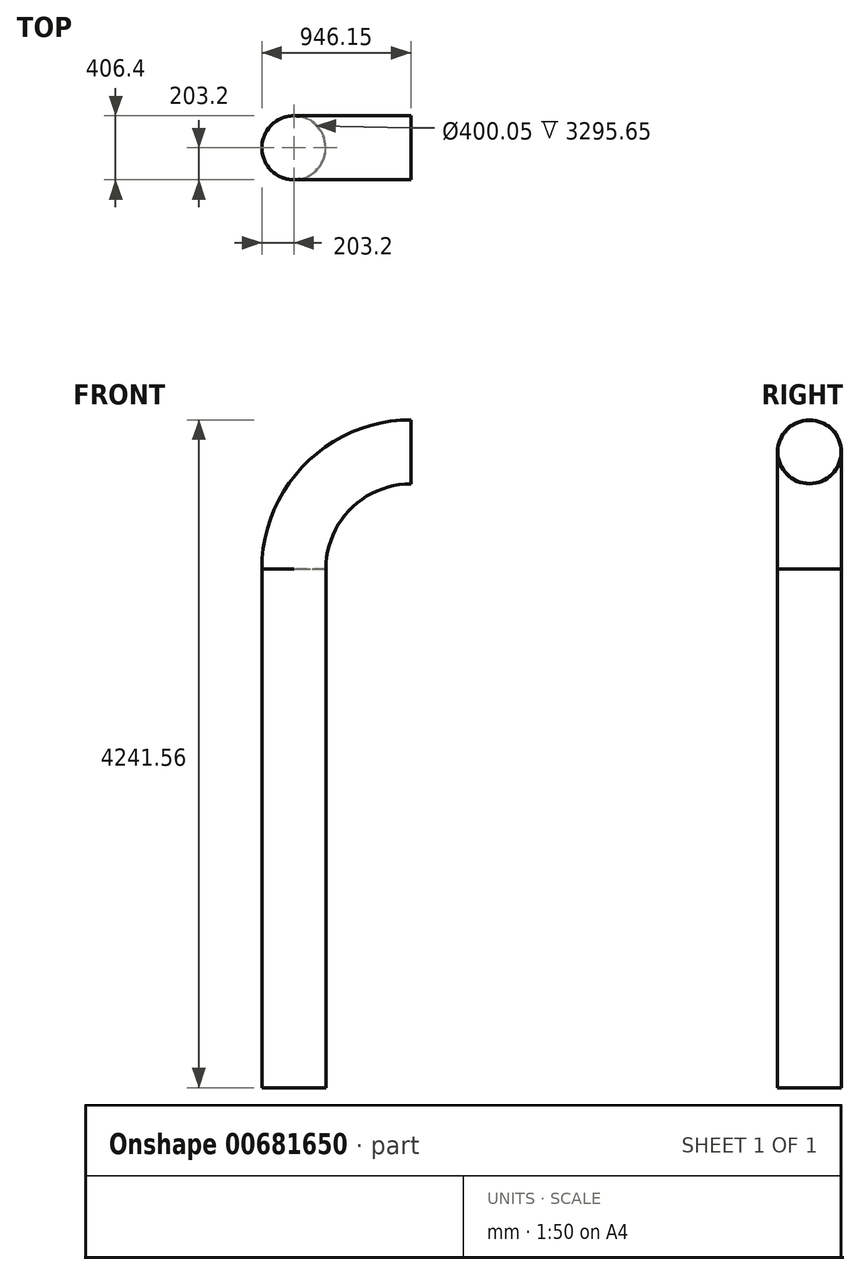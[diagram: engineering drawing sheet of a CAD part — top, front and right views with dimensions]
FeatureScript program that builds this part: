
annotation { "Feature Type Name" : "Feature", "Feature Type Description" : "" }
export const myFeature = defineFeature(function(context is Context, id is Id, definition is map)
    precondition{}
    {
        {
            var Q0;
            Q0=qCreatedBy(makeId("Front.planeOp"),FACE);
            var sketch = newSketch(context, id + "F0", { "sketchPlane" : qUnion([Q0])});
            skLineSegment(sketch, "E0", {"start": v(0, 0) * mm, "end": v(742.95, 0) * mm, "construction": true});
            skLineSegment(sketch, "E1.MirrorCS", {"start": v(742.95, 0) * mm, "end": v(742.95, -406.4) * mm, "construction": true});
            skLineSegment(sketch, "E2.MirrorCS", {"start": v(742.95, -203.2) * mm, "end": v(895.35, -203.2) * mm, "construction": true});
            skLineSegment(sketch, "E3.MirrorCS", {"start": v(0, -946.15) * mm, "end": v(203.2, -946.15) * mm, "construction": true});
            skLineSegment(sketch, "E4.MirrorCS", {"start": v(742.95, -406.4) * mm, "end": v(742.95, -946.15) * mm, "construction": true});
            skArc(sketch, "E5.MirrorCS", {"start": v(742.95, -203.2) * mm, "mid": v(217.6, -420.8) * mm, "end": v(0, -946.15) * mm, "construction": true});
            skLineSegment(sketch, "E6.MirrorCS", {"start": v(0, 0) * mm, "end": v(0, -946.15) * mm, "construction": true});
            skLineSegment(sketch, "E7.MirrorCS", {"start": v(0, -946.15) * mm, "end": v(0, -4241.8) * mm, "construction": true});
            skLineSegment(sketch, "E8", {"start": v(0, -4241.8) * mm, "end": v(203.2, -4241.8) * mm, "construction": true});
            skSolve(sketch);
        }
        {
            var Q0;
            Q0=sQuery(id+"F0.wireOp",EDGE,"E1.MirrorCS");
            cPlane(context, id + "F1", {"entities" : qUnion([Q0]), "cplaneType" : CPlaneType.LINE_ANGLE, "offset" : 25.4 * mm, "angle" : 0 * degree, "width" : 152.4 * mm, "height" : 152.4 * mm});
        }
        {
            var Q0;
            Q0=qCreatedBy(id+"F1.planeOp",FACE);
            var sketch = newSketch(context, id + "F2", { "sketchPlane" : qUnion([Q0])});
            skCircle(sketch, "E9", {"center": v(0, -203.44) * mm, "radius": 203.2 * mm});
            skCircle(sketch, "E10", {"center": v(0, -203.44) * mm, "radius": 200.03 * mm});
            skSolve(sketch);
        }
        {
            var Q0;
            Q0=sQuery(id+"F0.wireOp",EDGE,"E3.MirrorCS");
            cPlane(context, id + "F3", {"entities" : qUnion([Q0]), "cplaneType" : CPlaneType.LINE_ANGLE, "offset" : 25.4 * mm, "angle" : 90 * degree, "width" : 152.4 * mm, "height" : 152.4 * mm});
        }
        {
            var Q0;
            Q0=qCreatedBy(id+"F3.planeOp",FACE);
            var sketch = newSketch(context, id + "F4", { "sketchPlane" : qUnion([Q0])});
            skLineSegment(sketch, "E11", {"start": v(742.95, 0) * mm, "end": v(742.95, 154.8) * mm});
            skSolve(sketch);
        }
        {
            var Q0;
            Q0=makeQuery(id+"F2.imprint","IMPRINT",FACE,{"disambiguationData":[TD([[makeQuery(id+"F2.imprint","IMPRINT",EDGE,{"derivedFrom":sQuery(id+"F2.wireOp",EDGE,"E9")}),1.0]])]});
            var Q1;
            Q1=sQuery(id+"F4.wireOp",EDGE,"E11");
            revolve(context, id + "F5", {"surfaceOperationType" : NewSurfaceOperationType.NEW, "entities" : qUnion([Q0]), "axis" : qUnion([Q1]), "revolveType" : RevolveType.ONE_DIRECTION, "oppositeDirection" : true, "angle" : 90 * degree});
        }
        {
            var Q0;
            Q0=sQuery(id+"F0.wireOp",EDGE,"E8");
            cPlane(context, id + "F6", {"entities" : qUnion([Q0]), "cplaneType" : CPlaneType.LINE_ANGLE, "offset" : 25.4 * mm, "angle" : 90 * degree, "width" : 152.4 * mm, "height" : 152.4 * mm});
        }
        {
            var Q0;
            Q0=qCreatedBy(id+"F6.planeOp",FACE);
            var sketch = newSketch(context, id + "F7", { "sketchPlane" : qUnion([Q0])});
            skCircle(sketch, "E12", {"center": v(0, 0) * mm, "radius": 203.2 * mm});
            skCircle(sketch, "E13", {"center": v(0, 0) * mm, "radius": 200.03 * mm});
            skSolve(sketch);
        }
        {
            var Q0;
            Q0=makeQuery(id+"F7.imprint","IMPRINT",FACE,{"disambiguationData":[TD([[makeQuery(id+"F7.imprint","IMPRINT",EDGE,{"derivedFrom":sQuery(id+"F7.wireOp",EDGE,"E12")}),1.0]])]});
            extrude(context, id + "F8", {"entities" : qUnion([Q0]), "depth" : 3295.65 * mm, "offsetDistance" : 25.4 * mm});
        }
    });
